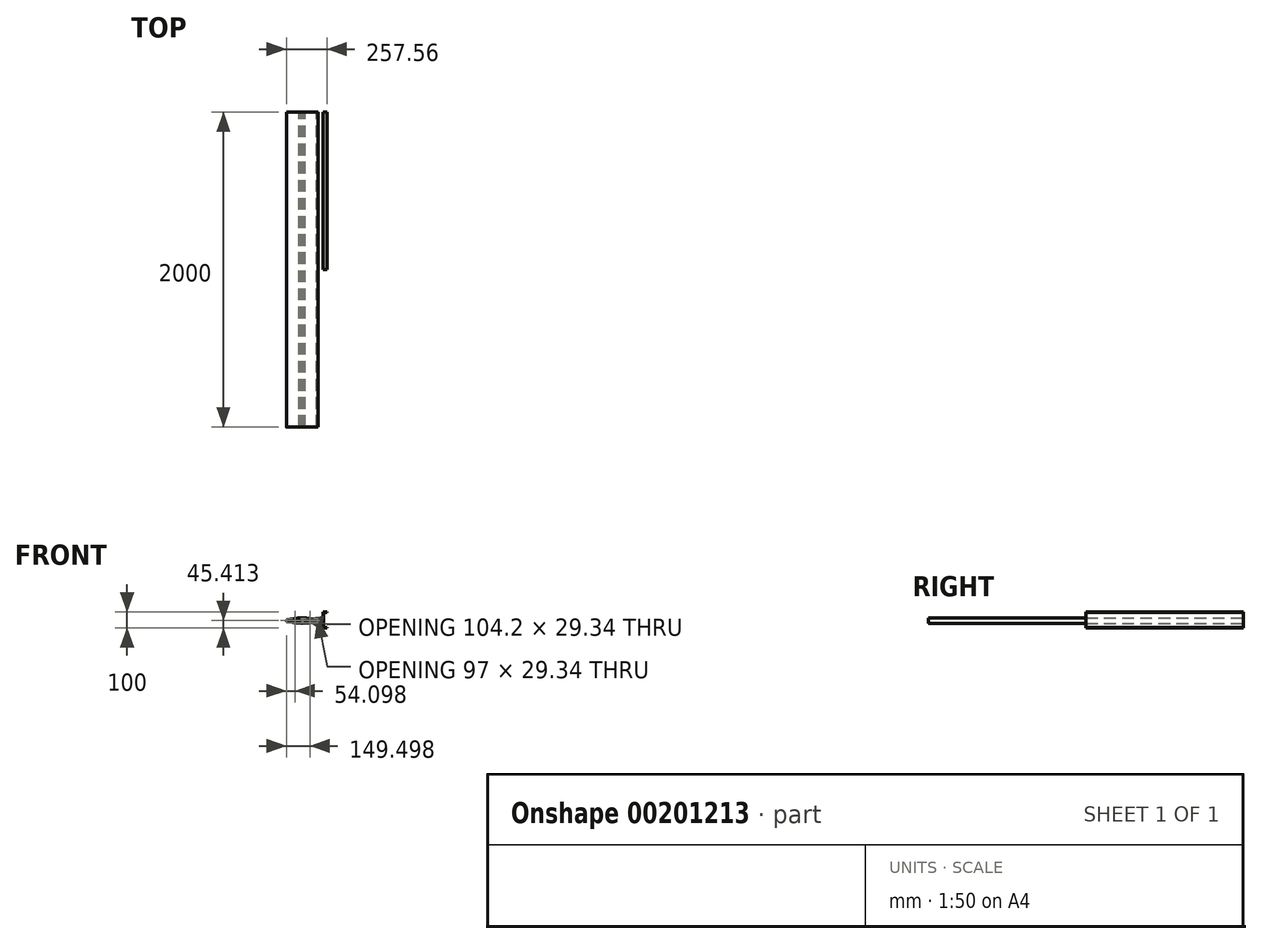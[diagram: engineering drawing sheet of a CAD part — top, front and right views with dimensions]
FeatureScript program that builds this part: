
annotation { "Feature Type Name" : "Feature", "Feature Type Description" : "" }
export const myFeature = defineFeature(function(context is Context, id is Id, definition is map)
    precondition{}
    {
        {
            var Q0;
            Q0=qCreatedBy(makeId("Front.planeOp"),FACE);
            var sketch = newSketch(context, id + "F0", { "sketchPlane" : qUnion([Q0])});
            skArc(sketch, "E0", {"start": v(-211.4, -7.96) * mm, "mid": v(-214.48, -11.97) * mm, "end": v(-211.4, -15.98) * mm});
            skArc(sketch, "E1", {"start": v(-208.9, -10.36) * mm, "mid": v(-212.48, -11.97) * mm, "end": v(-208.9, -13.58) * mm});
            skLineSegment(sketch, "E2", {"start": v(-113.48, -2.99) * mm, "end": v(-113.48, 1.7) * mm});
            skLineSegment(sketch, "E3", {"start": v(-115.48, -2.99) * mm, "end": v(-115.48, 1.7) * mm});
            skArc(sketch, "E4", {"start": v(-17.57, -7.96) * mm, "mid": v(-114.48, 4.7) * mm, "end": v(-211.4, -7.96) * mm});
            skArc(sketch, "E5", {"start": v(-22.07, -8.85) * mm, "mid": v(-66.92, -0.32) * mm, "end": v(-112.48, 2.7) * mm});
            skArc(sketch, "E6", {"start": v(-112.48, 2.7) * mm, "mid": v(-113.19, 2.41) * mm, "end": v(-113.48, 1.7) * mm});
            skArc(sketch, "E7", {"start": v(-116.49, 2.7) * mm, "mid": v(-120.54, 2.66) * mm, "end": v(-124.6, 2.57) * mm});
            skArc(sketch, "E8", {"start": v(-115.48, 1.7) * mm, "mid": v(-115.78, 2.41) * mm, "end": v(-116.49, 2.7) * mm});
            skArc(sketch, "E9", {"start": v(-124.6, 2.57) * mm, "mid": v(-125.38, 2.15) * mm, "end": v(-125.52, 1.27) * mm});
            skArc(sketch, "E10", {"start": v(-134.56, 2.17) * mm, "mid": v(-171, -1.57) * mm, "end": v(-206.9, -8.85) * mm});
            skArc(sketch, "E11", {"start": v(-133.53, 0.95) * mm, "mid": v(-133.74, 1.82) * mm, "end": v(-134.56, 2.17) * mm});
            skArc(sketch, "E12", {"start": v(-119.37, -15.78) * mm, "mid": v(-108.28, -11.97) * mm, "end": v(-119.37, -8.16) * mm});
            skArc(sketch, "E13", {"start": v(-120.95, -17) * mm, "mid": v(-118.87, -18.9) * mm, "end": v(-116.26, -19.97) * mm});
            skArc(sketch, "E14", {"start": v(-115.48, -20.95) * mm, "mid": v(-115.7, -20.32) * mm, "end": v(-116.26, -19.97) * mm});
            skArc(sketch, "E15", {"start": v(-112.7, -19.97) * mm, "mid": v(-108.2, -17.25) * mm, "end": v(-106.3, -12.36) * mm});
            skArc(sketch, "E16", {"start": v(-106.3, -11.58) * mm, "mid": v(-108.2, -6.69) * mm, "end": v(-112.7, -3.96) * mm});
            skArc(sketch, "E17", {"start": v(-112.7, -19.97) * mm, "mid": v(-113.26, -20.32) * mm, "end": v(-113.48, -20.95) * mm});
            skArc(sketch, "E18", {"start": v(-113.48, -2.99) * mm, "mid": v(-113.26, -3.61) * mm, "end": v(-112.7, -3.96) * mm});
            skArc(sketch, "E19", {"start": v(-116.26, -3.96) * mm, "mid": v(-118.87, -5.04) * mm, "end": v(-120.95, -6.93) * mm});
            skArc(sketch, "E20", {"start": v(-116.26, -3.96) * mm, "mid": v(-115.7, -3.61) * mm, "end": v(-115.48, -2.99) * mm});
            skArc(sketch, "E21", {"start": v(-120.95, -6.93) * mm, "mid": v(-120.78, -8.33) * mm, "end": v(-119.37, -8.16) * mm});
            skArc(sketch, "E22", {"start": v(-119.37, -15.78) * mm, "mid": v(-120.78, -15.6) * mm, "end": v(-120.95, -17) * mm});
            skArc(sketch, "E23", {"start": v(-127.87, -1.4) * mm, "mid": v(-129.48, 2.18) * mm, "end": v(-131.1, -1.4) * mm});
            skArc(sketch, "E24", {"start": v(-126.37, -2.72) * mm, "mid": v(-125.42, -0.83) * mm, "end": v(-125.52, 1.27) * mm});
            skArc(sketch, "E25", {"start": v(-133.53, 0.95) * mm, "mid": v(-133.5, -1) * mm, "end": v(-132.6, -2.72) * mm});
            skArc(sketch, "E26", {"start": v(-132.6, -2.72) * mm, "mid": v(-131.18, -2.8) * mm, "end": v(-131.1, -1.4) * mm});
            skArc(sketch, "E27", {"start": v(-127.87, -1.4) * mm, "mid": v(-127.79, -2.8) * mm, "end": v(-126.37, -2.72) * mm});
            skArc(sketch, "E28", {"start": v(-101.1, -22.54) * mm, "mid": v(-99.48, -26.12) * mm, "end": v(-97.87, -22.54) * mm});
            skArc(sketch, "E29", {"start": v(-102.6, -21.22) * mm, "mid": v(-103.54, -23.1) * mm, "end": v(-103.44, -25.2) * mm});
            skArc(sketch, "E30", {"start": v(-95.43, -24.88) * mm, "mid": v(-95.46, -22.94) * mm, "end": v(-96.37, -21.22) * mm});
            skArc(sketch, "E31", {"start": v(-95.43, -24.88) * mm, "mid": v(-95.22, -25.75) * mm, "end": v(-94.4, -26.1) * mm});
            skArc(sketch, "E32", {"start": v(-96.37, -21.22) * mm, "mid": v(-97.79, -21.13) * mm, "end": v(-97.87, -22.54) * mm});
            skArc(sketch, "E33", {"start": v(-101.1, -22.54) * mm, "mid": v(-101.18, -21.13) * mm, "end": v(-102.6, -21.22) * mm});
            skArc(sketch, "E34", {"start": v(-211.4, -15.98) * mm, "mid": v(-114.48, -28.64) * mm, "end": v(-17.57, -15.98) * mm});
            skArc(sketch, "E35", {"start": v(-206.9, -15.08) * mm, "mid": v(-162.04, -23.61) * mm, "end": v(-116.49, -26.64) * mm});
            skArc(sketch, "E36", {"start": v(-116.49, -26.64) * mm, "mid": v(-115.78, -26.35) * mm, "end": v(-115.48, -25.64) * mm});
            skLineSegment(sketch, "E37", {"start": v(-113.48, -20.95) * mm, "end": v(-113.48, -25.64) * mm});
            skLineSegment(sketch, "E38", {"start": v(-115.48, -20.95) * mm, "end": v(-115.48, -25.64) * mm});
            skArc(sketch, "E39", {"start": v(-112.48, -26.64) * mm, "mid": v(-108.42, -26.6) * mm, "end": v(-104.37, -26.5) * mm});
            skArc(sketch, "E40", {"start": v(-104.37, -26.5) * mm, "mid": v(-103.58, -26.09) * mm, "end": v(-103.44, -25.2) * mm});
            skArc(sketch, "E41", {"start": v(-113.48, -25.64) * mm, "mid": v(-113.19, -26.35) * mm, "end": v(-112.48, -26.64) * mm});
            skArc(sketch, "E42", {"start": v(-94.4, -26.1) * mm, "mid": v(-57.97, -22.36) * mm, "end": v(-22.07, -15.08) * mm});
            skArc(sketch, "E43", {"start": v(-208.9, -10.36) * mm, "mid": v(-207.75, -10.48) * mm, "end": v(-207.26, -9.43) * mm});
            skArc(sketch, "E44", {"start": v(-206.9, -8.85) * mm, "mid": v(-207.2, -9.07) * mm, "end": v(-207.26, -9.43) * mm});
            skArc(sketch, "E45", {"start": v(-207.26, -14.5) * mm, "mid": v(-207.75, -13.46) * mm, "end": v(-208.9, -13.58) * mm});
            skArc(sketch, "E46", {"start": v(-207.26, -14.5) * mm, "mid": v(-207.2, -14.87) * mm, "end": v(-206.9, -15.08) * mm});
            skArc(sketch, "E47", {"start": v(-17.57, -15.98) * mm, "mid": v(-14.48, -11.97) * mm, "end": v(-17.57, -7.96) * mm});
            skArc(sketch, "E48", {"start": v(-20.06, -13.58) * mm, "mid": v(-16.48, -11.97) * mm, "end": v(-20.06, -10.36) * mm});
            skArc(sketch, "E49", {"start": v(-21.7, -9.43) * mm, "mid": v(-21.21, -10.48) * mm, "end": v(-20.06, -10.36) * mm});
            skArc(sketch, "E50", {"start": v(-21.7, -9.43) * mm, "mid": v(-21.77, -9.07) * mm, "end": v(-22.07, -8.85) * mm});
            skArc(sketch, "E51", {"start": v(-20.06, -13.58) * mm, "mid": v(-21.21, -13.46) * mm, "end": v(-21.7, -14.5) * mm});
            skArc(sketch, "E52", {"start": v(-22.07, -15.08) * mm, "mid": v(-21.77, -14.87) * mm, "end": v(-21.7, -14.5) * mm});
            skLineSegment(sketch, "E53", {"start": v(-106.68, -11.97) * mm, "end": v(-106.3, -11.58) * mm});
            skLineSegment(sketch, "E54", {"start": v(-106.68, -11.97) * mm, "end": v(-106.3, -12.36) * mm});
            skSolve(sketch);
        }
        {
            var Q0;
            Q0=makeQuery(id+"F0.imprint","IMPRINT",FACE,{"disambiguationData":[TD([[makeQuery(id+"F0.imprint","IMPRINT",EDGE,{"derivedFrom":sQuery(id+"F0.wireOp",EDGE,"E0")}),1.0]])]});
            extrude(context, id + "F1", {"entities" : qUnion([Q0]), "depth" : 2000 * mm});
        }
        {
            var Q0;
            Q0=qCreatedBy(makeId("Front.planeOp"),FACE);
            var sketch = newSketch(context, id + "F2", { "sketchPlane" : qUnion([Q0])});
            skLineSegment(sketch, "E55.bottom", {"start": v(18.08, 42.62) * mm, "end": v(43.08, 42.62) * mm});
            skLineSegment(sketch, "E55.top", {"start": v(18.08, -57.38) * mm, "end": v(43.08, -57.38) * mm});
            skLineSegment(sketch, "E55.left", {"start": v(18.08, 42.62) * mm, "end": v(18.08, -57.38) * mm});
            skLineSegment(sketch, "E56.0", {"start": v(21.08, -54.38) * mm, "end": v(43.08, -54.38) * mm});
            skPoint(sketch, "E57.orphan", {"position": v(21.08, -57.37) * mm});
            skLineSegment(sketch, "E58", {"start": v(43.08, -54.38) * mm, "end": v(43.08, -57.38) * mm});
            skLineSegment(sketch, "E59", {"start": v(43.08, 42.62) * mm, "end": v(43.08, 39.62) * mm});
            skLineSegment(sketch, "E60", {"start": v(21.08, 39.62) * mm, "end": v(43.08, 39.62) * mm});
            skLineSegment(sketch, "E61", {"start": v(21.08, 39.62) * mm, "end": v(21.08, -54.38) * mm});
            skSolve(sketch);
        }
        {
            var Q0;
            Q0=makeQuery(id+"F2.imprint","IMPRINT",FACE,{"disambiguationData":[TD([[makeQuery(id+"F2.imprint","IMPRINT",EDGE,{"derivedFrom":sQuery(id+"F2.wireOp",EDGE,"E55.bottom")}),-1.0]])]});
            extrude(context, id + "F3", {"entities" : qUnion([Q0]), "depth" : 1000 * mm});
        }
    });
